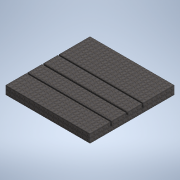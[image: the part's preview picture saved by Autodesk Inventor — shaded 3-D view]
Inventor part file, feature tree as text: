
AUTODESK INVENTOR PART (.ipt)
format: ipt  version: 2022 (Build 260153000, 153)  size: 194,048 bytes
history: native  units: in
note: dims shown in document units (in); Inventor stores cm internally (conversion verified against a paired STEP export)
features: extrude x3, sketch x3
ambient origin geometry x8: Origin, YZ Plane, XZ Plane, XY Plane, X Axis, Y Axis, Z Axis, Center Point
bodies: Solid1 (feature_tree)
feature tree (6):
  extrude  "Extrusion1"  Depth=157.4803in
  extrude  "Extrusion2"  Depth=15.748in TaperAngle=0.0deg
  extrude  "Extrusion3"  Depth=59.0551in
  sketch  "Sketch1"  dims[d1=157.4803in d2=157.4803in]
  sketch  "Sketch2"  dims[d3=157.4803in d4=15.748in d5=0.0in]
  sketch  "Sketch3"  dims[d6=39.3701in d7=59.0551in d8=1.1811in d9=3.5433in d10=0.3937in d11=5.315in d12=3.1496in d13=0.3937in d14=0.3937in d15=0.315in d16=1.5748in d17=0.1969in d18=0.1969in d19=0.1969in d20=1.1811in d21=2.3622in d22=3.5433in d23=0.3937in d24=5.315in d25=0.3937in d26=0.315in d27=1.5748in d28=0.1969in d29=0.1969in d30=0.3937in d31=157.4803in d32=0.0in d33=68.8976in d34=1.2795in d35=2.5591in d36=1.7717in d37=1.1811in d38=4.1339in d39=4.9213in d40=1.1811in d41=157.4803in d42=0.0in]
